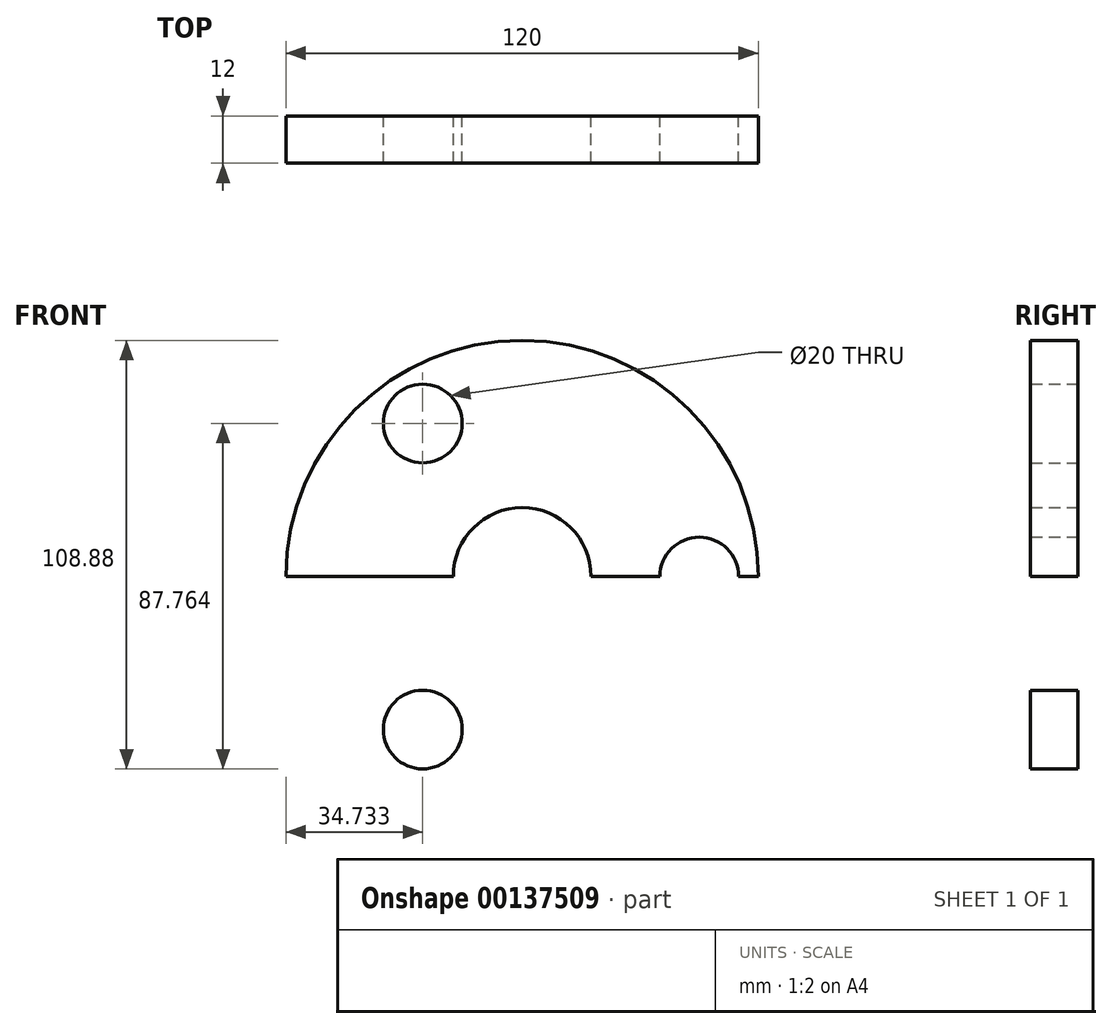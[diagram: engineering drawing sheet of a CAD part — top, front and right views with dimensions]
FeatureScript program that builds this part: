
annotation { "Feature Type Name" : "Feature", "Feature Type Description" : "" }
export const myFeature = defineFeature(function(context is Context, id is Id, definition is map)
    precondition{}
    {
        {
            var Q0;
            Q0=qCreatedBy(makeId("Front.planeOp"),FACE);
            var sketch = newSketch(context, id + "F0", { "sketchPlane" : qUnion([Q0])});
            skCircle(sketch, "E0", {"center": v(0, 0) * mm, "radius": 60 * mm});
            skCircle(sketch, "E1", {"center": v(0, 0) * mm, "radius": 17.5 * mm});
            skPoint(sketch, "E2.orphan", {"position": v(-26.59, -48.24) * mm});
            skPoint(sketch, "E3.orphan", {"position": v(39.96, -39.98) * mm});
            skPoint(sketch, "E4", {"position": v(-12.07, -21.9) * mm});
            skPoint(sketch, "E5", {"position": v(27.4, -27.4) * mm});
            skPoint(sketch, "E6.orphan", {"position": v(12.37, -12.38) * mm});
            skPoint(sketch, "E7.MirrorCS.end.orphan", {"position": v(42.42, -42.44) * mm});
            skPoint(sketch, "E8", {"position": v(38.48, 0) * mm});
            skPoint(sketch, "E9.trimOffspring.end.orphan", {"position": v(59.88, 3.83) * mm});
            skPoint(sketch, "E10.start.orphan", {"position": v(17.08, -3.83) * mm});
            skLineSegment(sketch, "E11", {"start": v(0, 0) * mm, "end": v(38.48, 0) * mm});
            skLineSegment(sketch, "E12", {"start": v(60, 0) * mm, "end": v(33.25, 0) * mm});
            skCircle(sketch, "E13", {"center": v(45, 0) * mm, "radius": 10 * mm});
            skCircle(sketch, "E14.MirrorC", {"center": v(-25.27, -38.88) * mm, "radius": 10 * mm});
            skCircle(sketch, "E15.MirrorC", {"center": v(-25.27, 38.88) * mm, "radius": 10 * mm});
            skLineSegment(sketch, "E16.trimOffspring", {"start": v(17.5, 0) * mm, "end": v(-60, 0) * mm});
            skLineSegment(sketch, "E17.trimOffspring", {"start": v(38.48, 0) * mm, "end": v(23.39, 0) * mm});
            skLineSegment(sketch, "E18.trimOffspring", {"start": v(33.25, 0) * mm, "end": v(55, 0) * mm});
            skLineSegment(sketch, "E19", {"start": v(0, 0) * mm, "end": v(35, 0) * mm});
            skSolve(sketch);
        }
        {
            var Q0;
            Q0=makeQuery(id+"F0.imprint","IMPRINT",FACE,{"disambiguationData":[TD([[makeQuery(id+"F0.imprint","IMPRINT",EDGE,{"derivedFrom":sQuery(id+"F0.wireOp",EDGE,"E14.MirrorC")}),1.0]])]});
            var Q1;
            Q1=makeQuery(id+"F0.imprint","IMPRINT",FACE,{"disambiguationData":[TD([[makeQuery(id+"F0.imprint","IMPRINT",EDGE,{"derivedFrom":sQuery(id+"F0.wireOp",EDGE,"E15.MirrorC")}),-1.0]])]});
            extrude(context, id + "F1", {"entities" : qUnion([Q0, Q1]), "depth" : 12 * mm, "symmetric" : true});
        }
    });
